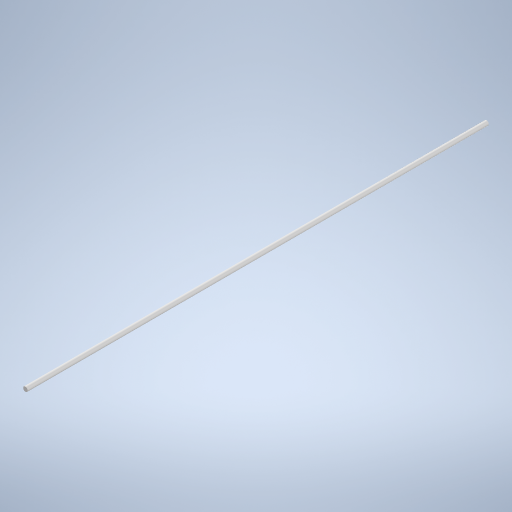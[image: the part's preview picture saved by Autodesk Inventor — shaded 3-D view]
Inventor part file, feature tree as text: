
AUTODESK INVENTOR PART (.ipt)
format: ipt  version: 2023 (Build 270158000, 158)  size: 239,104 bytes
history: native  units: in
note: dims shown in document units (in); Inventor stores cm internally (conversion verified against a paired STEP export)
features: extrude x2, sketch x2
ambient origin geometry x8: Origin, YZ Plane, XZ Plane, XY Plane, X Axis, Y Axis, Z Axis, Center Point
bodies: Solid1 (feature_tree)
feature tree (4):
  extrude  "Extrusion1"  Depth=39.3701in TaperAngle=0.0deg
  extrude  "Extrusion2"  [1 undecoded]
  sketch  "Sketch1"  dims[d0=0.5906in d1=39.3701in d2=0.0in]
  sketch  "Sketch2"  dims[d3=19.685in d4=0.0in]
note: 1 required parameter value undecoded (feature->parameter linkage not recoverable at this tier; creation-order binding heuristic only, values carry confidence <= 0.55)
